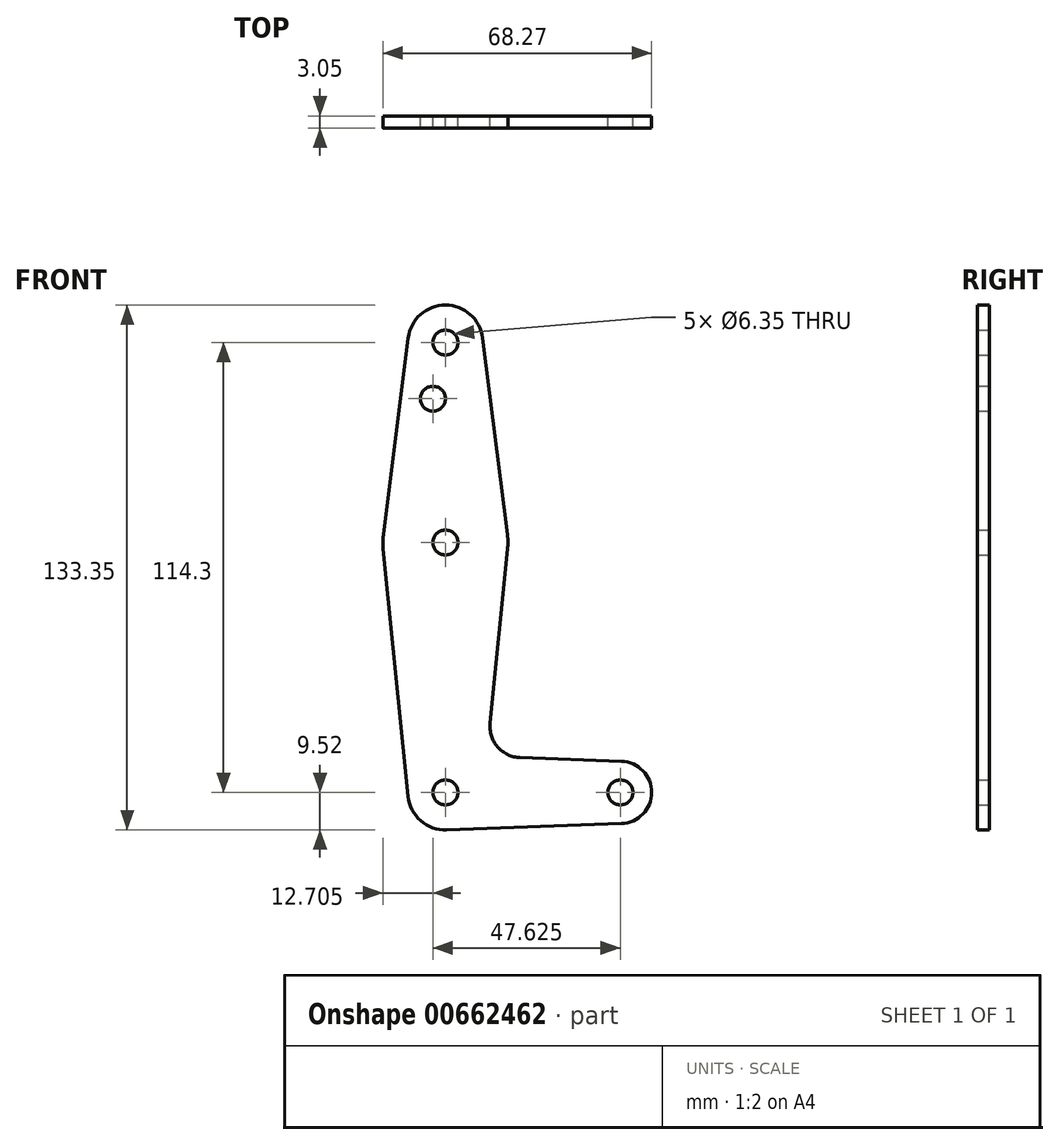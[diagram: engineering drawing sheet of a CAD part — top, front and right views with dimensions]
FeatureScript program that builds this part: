
annotation { "Feature Type Name" : "Feature", "Feature Type Description" : "" }
export const myFeature = defineFeature(function(context is Context, id is Id, definition is map)
    precondition{}
    {
        {
            var Q0;
            Q0=qCreatedBy(makeId("Front.planeOp"),FACE);
            var sketch = newSketch(context, id + "F0", { "sketchPlane" : qUnion([Q0])});
            skCircle(sketch, "E0", {"center": v(0, 0) * mm, "radius": 9.53 * mm});
            skCircle(sketch, "E1", {"center": v(0, 63.5) * mm, "radius": 15.88 * mm});
            skCircle(sketch, "E2", {"center": v(0, 114.3) * mm, "radius": 9.53 * mm});
            skCircle(sketch, "E3", {"center": v(44.45, 0) * mm, "radius": 7.94 * mm});
            skLineSegment(sketch, "E4", {"start": v(0, 63.5) * mm, "end": v(0, 0) * mm, "construction": true});
            skLineSegment(sketch, "E5", {"start": v(0, 0) * mm, "end": v(44.45, 0) * mm, "construction": true});
            skLineSegment(sketch, "E6", {"start": v(0, 63.5) * mm, "end": v(0, 114.3) * mm, "construction": true});
            skLineSegment(sketch, "E7", {"start": v(-9.45, 115.5) * mm, "end": v(-15.75, 65.48) * mm});
            skLineSegment(sketch, "E8", {"start": v(9.45, 115.5) * mm, "end": v(15.75, 65.48) * mm});
            skLineSegment(sketch, "E9", {"start": v(-15.8, 61.91) * mm, "end": v(-9.48, -0.95) * mm});
            skLineSegment(sketch, "E10", {"start": v(11.34, 17.6) * mm, "end": v(15.8, 61.91) * mm});
            skLineSegment(sketch, "E11", {"start": v(0.34, -9.52) * mm, "end": v(44.73, -7.93) * mm});
            skLineSegment(sketch, "E12", {"start": v(44.73, 7.93) * mm, "end": v(18.97, 8.85) * mm});
            skCircle(sketch, "E13", {"center": v(0, 114.3) * mm, "radius": 3.18 * mm});
            skCircle(sketch, "E14", {"center": v(0, 63.5) * mm, "radius": 3.18 * mm});
            skCircle(sketch, "E15", {"center": v(0, 0) * mm, "radius": 3.18 * mm});
            skCircle(sketch, "E16", {"center": v(44.45, 0) * mm, "radius": 3.18 * mm});
            skCircle(sketch, "E17", {"center": v(-3.18, 100.03) * mm, "radius": 3.18 * mm});
            skArc(sketch, "E18.filletArc", {"start": v(11.34, 17.6) * mm, "mid": v(13.26, 11.57) * mm, "end": v(18.97, 8.85) * mm});
            skSolve(sketch);
        }
        {
            var Q0;
            Q0=makeQuery(id+"F0.imprint","IMPRINT",FACE,{"disambiguationData":[TD([[makeQuery(id+"F0.imprint","IMPRINT",EDGE,{"derivedFrom":sQuery(id+"F0.wireOp",EDGE,"E13")}),-1.0]])]});
            var Q1;
            {var subQ1=sQuery(id+"F0.wireOp",EDGE,"E7");Q1=makeQuery(id+"F0.imprint","IMPRINT",FACE,{"disambiguationData":[TD([[makeQuery(id+"F0.imprint","IMPRINT",EDGE,{"derivedFrom":subQ1}),1.0]])]});}
            var Q2;
            Q2=makeQuery(id+"F0.imprint","IMPRINT",FACE,{"disambiguationData":[TD([[makeQuery(id+"F0.imprint","IMPRINT",EDGE,{"derivedFrom":sQuery(id+"F0.wireOp",EDGE,"E14")}),-1.0]])]});
            var Q3;
            {var subQ0=sQuery(id+"F0.wireOp",EDGE,"E9");Q3=makeQuery(id+"F0.imprint","IMPRINT",FACE,{"disambiguationData":[TD([[makeQuery(id+"F0.imprint","IMPRINT",EDGE,{"derivedFrom":subQ0}),1.0]])]});}
            var Q4;
            Q4=makeQuery(id+"F0.imprint","IMPRINT",FACE,{"disambiguationData":[TD([[makeQuery(id+"F0.imprint","IMPRINT",EDGE,{"derivedFrom":sQuery(id+"F0.wireOp",EDGE,"E15")}),-1.0]])]});
            var Q5;
            Q5=makeQuery(id+"F0.imprint","IMPRINT",FACE,{"disambiguationData":[TD([[makeQuery(id+"F0.imprint","IMPRINT",EDGE,{"derivedFrom":sQuery(id+"F0.wireOp",EDGE,"E16")}),-1.0]])]});
            extrude(context, id + "F1", {"entities" : qUnion([Q0, Q1, Q2, Q3, Q4, Q5]), "depth" : 3.05 * mm, "offsetDistance" : 25.4 * mm});
        }
    });
